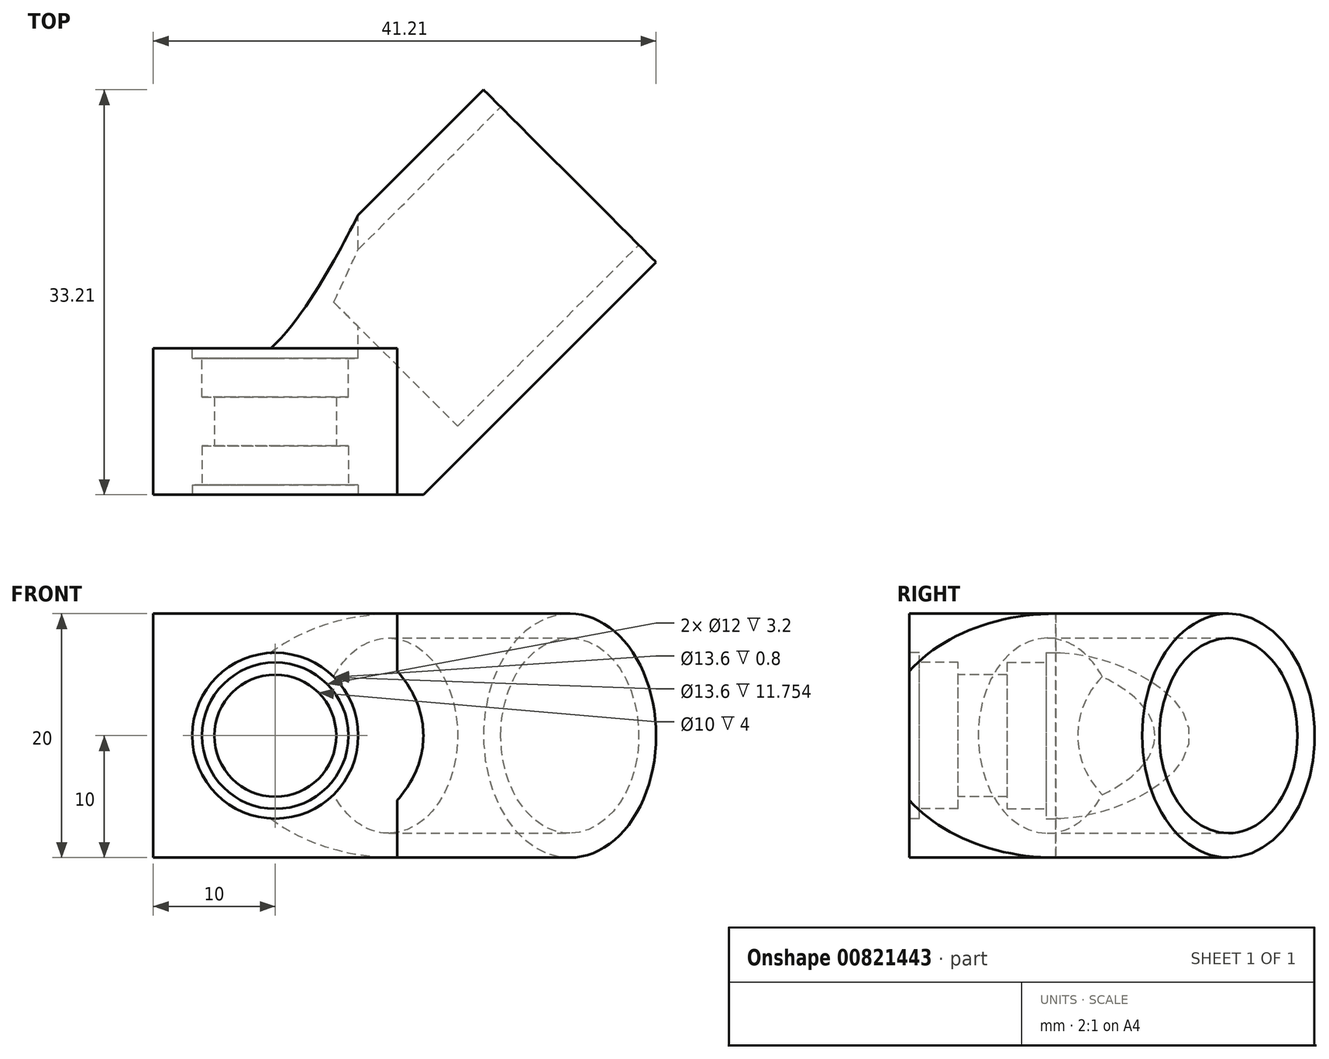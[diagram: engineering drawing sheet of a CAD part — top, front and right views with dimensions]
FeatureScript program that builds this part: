
annotation { "Feature Type Name" : "Feature", "Feature Type Description" : "" }
export const myFeature = defineFeature(function(context is Context, id is Id, definition is map)
    precondition{}
    {
        {
            var Q0;
            Q0=qCreatedBy(makeId("Front.planeOp"),FACE);
            var sketch = newSketch(context, id + "F0", { "sketchPlane" : qUnion([Q0])});
            skLineSegment(sketch, "E0.bottom", {"start": v(10, -10) * mm, "end": v(-10, -10) * mm});
            skLineSegment(sketch, "E0.top", {"start": v(10, 10) * mm, "end": v(-10, 10) * mm});
            skLineSegment(sketch, "E0.left", {"start": v(10, -10) * mm, "end": v(10, 10) * mm});
            skLineSegment(sketch, "E0.right", {"start": v(-10, -10) * mm, "end": v(-10, 10) * mm});
            skPoint(sketch, "E0.middle", {"position": v(0, 0) * mm});
            skSolve(sketch);
        }
        {
            var Q0;
            Q0 = qSketchRegion(id + "F0", true);
            extrude(context, id + "F1", {"entities" : qUnion([Q0]), "depth" : 12 * mm, "offsetDistance" : 25 * mm});
        }
        {
            var Q0;
            Q0=qCreatedBy(makeId("Right.planeOp"),FACE);
            var Q1;
            Q1=makeQuery(id+"F1.opExtrude","CAP_EDGE",EDGE,{"disambiguationData":[OSD([sQuery(id+"F0.wireOp",EDGE,"E0.left")])],"isStart":true});
            cPlane(context, id + "F2", {"entities" : qUnion([Q0, Q1]), "cplaneType" : CPlaneType.LINE_ANGLE, "offset" : 25 * mm, "angle" : 45 * degree, "width" : 150 * mm, "height" : 150 * mm});
        }
        {
            var Q0;
            Q0=qCreatedBy(id+"F2.planeOp",FACE);
            var sketch = newSketch(context, id + "F3", { "sketchPlane" : qUnion([Q0])});
            skCircle(sketch, "E1", {"center": v(7.07, 0) * mm, "radius": 10 * mm});
            skSolve(sketch);
        }
        {
            var Q0;
            Q0 = qSketchRegion(id + "F3", true);
            extrude(context, id + "F4", {"entities" : qUnion([Q0]), "operationType" : NewBodyOperationType.ADD, "oppositeDirection" : true, "depth" : 20 * mm, "offsetDistance" : 25 * mm, "hasSecondDirection" : true, "secondDirectionOppositeDirection" : false, "secondDirectionDepth" : 9 * mm});
        }
        {
            var Q0;
            Q0=makeQuery(id+"F1.opExtrude","CAP_FACE",FACE,{"disambiguationData":[OSD([sQuery(id+"F0.wireOp",EDGE,"E0.bottom"),sQuery(id+"F0.wireOp",EDGE,"E0.top"),sQuery(id+"F0.wireOp",EDGE,"E0.left"),sQuery(id+"F0.wireOp",EDGE,"E0.right")])],"isStart":false});
            var sketch = newSketch(context, id + "F5", { "sketchPlane" : qUnion([Q0])});
            skCircle(sketch, "E2", {"center": v(0, 0) * mm, "radius": 6.8 * mm});
            skSolve(sketch);
        }
        {
            var Q0;
            Q0 = qSketchRegion(id + "F5", true);
            extrude(context, id + "F6", {"entities" : qUnion([Q0]), "operationType" : NewBodyOperationType.REMOVE, "oppositeDirection" : true, "depth" : 0.8 * mm, "offsetDistance" : 25 * mm});
        }
        {
            var Q0;
            Q0=makeQuery(id+"F1.opExtrude","CAP_FACE",FACE,{"disambiguationData":[OSD([sQuery(id+"F0.wireOp",EDGE,"E0.bottom"),sQuery(id+"F0.wireOp",EDGE,"E0.top"),sQuery(id+"F0.wireOp",EDGE,"E0.left"),sQuery(id+"F0.wireOp",EDGE,"E0.right")])],"isStart":true});
            var sketch = newSketch(context, id + "F7", { "sketchPlane" : qUnion([Q0])});
            skCircle(sketch, "E3", {"center": v(0, 0) * mm, "radius": 6.8 * mm});
            skSolve(sketch);
        }
        {
            var Q0;
            Q0 = qSketchRegion(id + "F7", true);
            extrude(context, id + "F8", {"entities" : qUnion([Q0]), "operationType" : NewBodyOperationType.REMOVE, "oppositeDirection" : true, "depth" : 0.8 * mm, "offsetDistance" : 25 * mm, "hasSecondDirection" : true, "secondDirectionOppositeDirection" : false, "secondDirectionDepth" : 25 * mm});
        }
        {
            var Q0;
            Q0=makeQuery(id+"F8.boolean.opBoolean","COPY",FACE,{"derivedFrom":makeQuery(id+"F8.opExtrude","CAP_FACE",FACE,{"disambiguationData":[OSD([sQuery(id+"F7.wireOp",EDGE,"E3")])],"isStart":false})});
            var sketch = newSketch(context, id + "F9", { "sketchPlane" : qUnion([Q0])});
            skCircle(sketch, "E4", {"center": v(0, 0) * mm, "radius": 6 * mm});
            skSolve(sketch);
        }
        {
            var Q0;
            Q0 = qSketchRegion(id + "F9", true);
            extrude(context, id + "F10", {"entities" : qUnion([Q0]), "operationType" : NewBodyOperationType.REMOVE, "oppositeDirection" : true, "depth" : 3.2 * mm, "offsetDistance" : 25 * mm});
        }
        {
            var Q0;
            Q0=makeQuery(id+"F6.boolean.opBoolean","COPY",FACE,{"derivedFrom":makeQuery(id+"F6.opExtrude","CAP_FACE",FACE,{"disambiguationData":[OSD([sQuery(id+"F5.wireOp",EDGE,"E2")])],"isStart":false})});
            var sketch = newSketch(context, id + "F11", { "sketchPlane" : qUnion([Q0])});
            skCircle(sketch, "E5", {"center": v(0, 0) * mm, "radius": 6 * mm});
            skSolve(sketch);
        }
        {
            var Q0;
            Q0 = qSketchRegion(id + "F11", true);
            extrude(context, id + "F12", {"entities" : qUnion([Q0]), "operationType" : NewBodyOperationType.REMOVE, "oppositeDirection" : true, "depth" : 3.2 * mm, "offsetDistance" : 25 * mm});
        }
        {
            var Q0;
            Q0=makeQuery(id+"F12.boolean.opBoolean","COPY",FACE,{"derivedFrom":makeQuery(id+"F12.opExtrude","CAP_FACE",FACE,{"disambiguationData":[OSD([sQuery(id+"F11.wireOp",EDGE,"E5")])],"isStart":false})});
            var sketch = newSketch(context, id + "F13", { "sketchPlane" : qUnion([Q0])});
            skCircle(sketch, "E6", {"center": v(0, 0) * mm, "radius": 5 * mm});
            skSolve(sketch);
        }
        {
            var Q0;
            Q0 = qSketchRegion(id + "F13", true);
            extrude(context, id + "F14", {"entities" : qUnion([Q0]), "operationType" : NewBodyOperationType.REMOVE, "endBound" : BoundingType.UP_TO_NEXT, "oppositeDirection" : true, "depth" : 25 * mm, "offsetDistance" : 25 * mm});
        }
        {
            var Q0;
            Q0=qCreatedBy(makeId("Right.planeOp"),FACE);
            var sketch = newSketch(context, id + "F15", { "sketchPlane" : qUnion([Q0])});
            skLineSegment(sketch, "E7.bottom", {"start": v(-12, 10) * mm, "end": v(-18.59, 10) * mm});
            skLineSegment(sketch, "E7.top", {"start": v(-12, -10) * mm, "end": v(-18.59, -10) * mm});
            skLineSegment(sketch, "E7.left", {"start": v(-12, 10) * mm, "end": v(-12, -10) * mm});
            skLineSegment(sketch, "E7.right", {"start": v(-18.59, 10) * mm, "end": v(-18.59, -10) * mm});
            skSolve(sketch);
        }
        {
            var Q0;
            Q0 = qSketchRegion(id + "F15", true);
            extrude(context, id + "F16", {"entities" : qUnion([Q0]), "operationType" : NewBodyOperationType.REMOVE, "depth" : 25 * mm, "offsetDistance" : 25 * mm});
        }
        {
            var Q0;
            Q0=makeQuery(id+"F4.opExtrude","CAP_FACE",FACE,{"disambiguationData":[OSD([sQuery(id+"F3.wireOp",EDGE,"E1")])],"isStart":false});
            var sketch = newSketch(context, id + "F17", { "sketchPlane" : qUnion([Q0])});
            skCircle(sketch, "E8", {"center": v(-7.07, 0) * mm, "radius": 8 * mm});
            skSolve(sketch);
        }
        {
            var Q0;
            Q0 = qSketchRegion(id + "F17", true);
            extrude(context, id + "F18", {"entities" : qUnion([Q0]), "operationType" : NewBodyOperationType.REMOVE, "oppositeDirection" : true, "depth" : 21 * mm, "offsetDistance" : 25 * mm});
        }
    });
